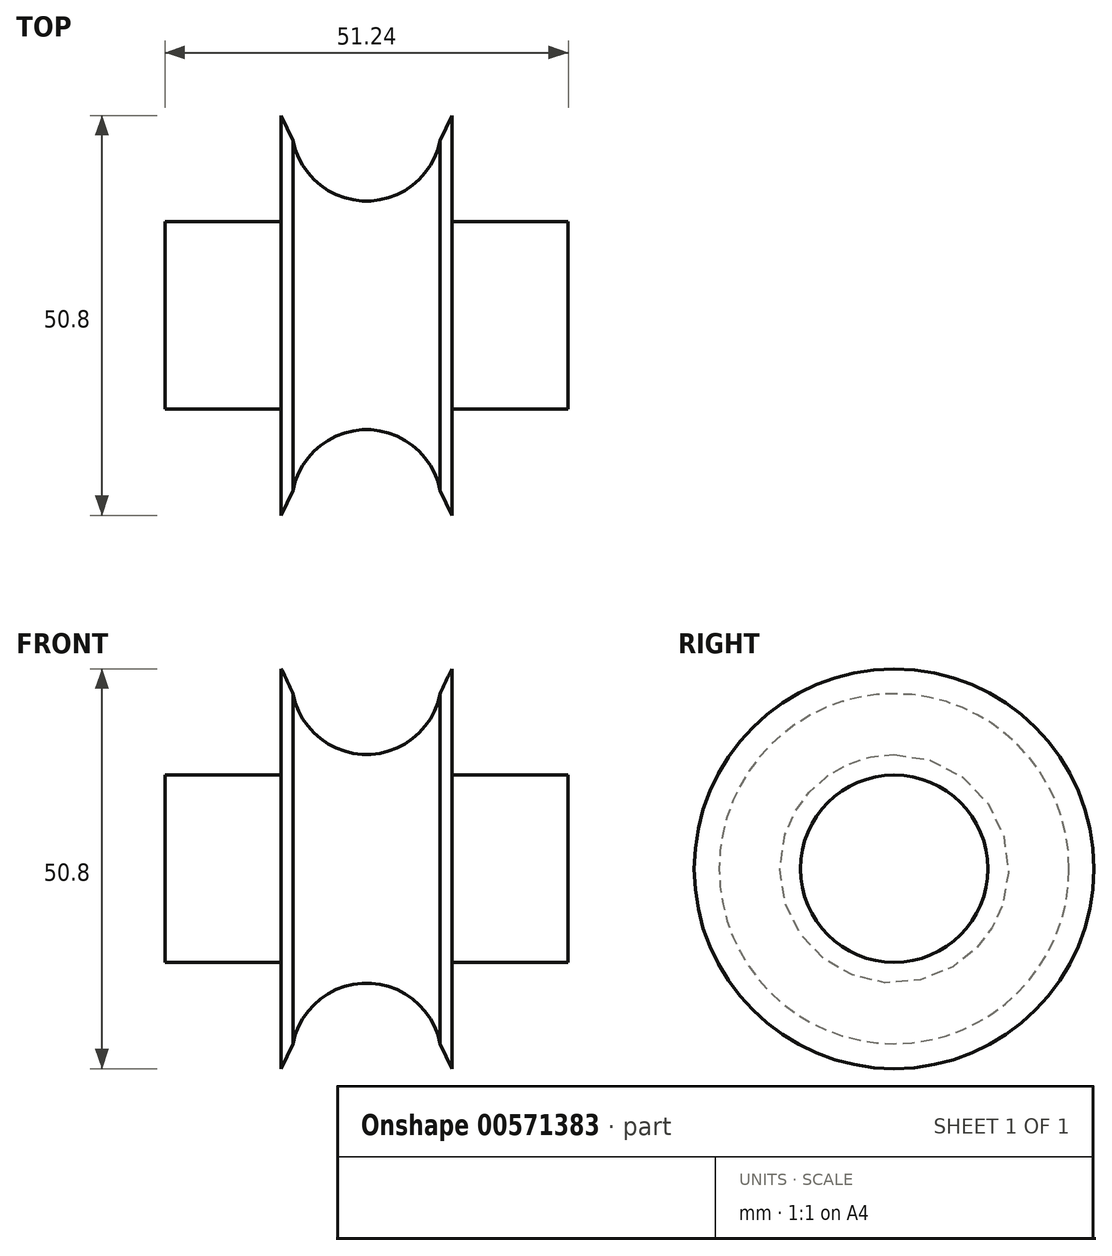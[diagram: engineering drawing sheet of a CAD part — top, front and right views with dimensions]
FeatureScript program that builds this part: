
annotation { "Feature Type Name" : "Feature", "Feature Type Description" : "" }
export const myFeature = defineFeature(function(context is Context, id is Id, definition is map)
    precondition{}
    {
        {
            var Q0;
            Q0=qCreatedBy(makeId("Front.planeOp"),FACE);
            var sketch = newSketch(context, id + "F0", { "sketchPlane" : qUnion([Q0])});
            skLineSegment(sketch, "E0", {"start": v(-10.83, 0) * mm, "end": v(0, 0) * mm});
            skLineSegment(sketch, "E1", {"start": v(-10.83, 25.4) * mm, "end": v(-10.83, 0) * mm});
            skLineSegment(sketch, "E2", {"start": v(-10.83, 11.9) * mm, "end": v(-25.62, 11.9) * mm});
            skLineSegment(sketch, "E3", {"start": v(-25.62, 11.9) * mm, "end": v(-25.62, 0) * mm});
            skLineSegment(sketch, "E4", {"start": v(-25.62, 0) * mm, "end": v(0, 0) * mm});
            skLineSegment(sketch, "E5", {"start": v(-10.83, 25.4) * mm, "end": v(-9.35, 22.23) * mm});
            skLineSegment(sketch, "E6.MirrorCS", {"start": v(25.62, 11.9) * mm, "end": v(25.62, 0) * mm});
            skLineSegment(sketch, "E7.MirrorCS", {"start": v(10.83, 11.9) * mm, "end": v(25.62, 11.9) * mm});
            skLineSegment(sketch, "E8.MirrorCS", {"start": v(10.83, 25.4) * mm, "end": v(10.83, 0) * mm});
            skLineSegment(sketch, "E9.MirrorCS", {"start": v(10.83, 25.4) * mm, "end": v(9.35, 22.23) * mm});
            skLineSegment(sketch, "E10.MirrorCS", {"start": v(25.62, 0) * mm, "end": v(0, 0) * mm});
            skArc(sketch, "E11", {"start": v(-9.35, 22.23) * mm, "mid": v(0, 14.52) * mm, "end": v(9.35, 22.23) * mm});
            skLineSegment(sketch, "E12", {"start": v(-37.22, 0) * mm, "end": v(46.88, 0) * mm, "construction": true});
            skSolve(sketch);
        }
        {
            var Q0;
            {var subQ0=sQuery(id+"F0.wireOp",EDGE,"E5");Q0=makeQuery(id+"F0.imprint","IMPRINT",FACE,{"disambiguationData":[TD([[makeQuery(id+"F0.imprint","IMPRINT",EDGE,{"derivedFrom":subQ0}),-1.0]])]});}
            var Q1;
            {var subQ0=sQuery(id+"F0.wireOp",EDGE,"E6.MirrorCS");Q1=makeQuery(id+"F0.imprint","IMPRINT",FACE,{"disambiguationData":[TD([[makeQuery(id+"F0.imprint","IMPRINT",EDGE,{"derivedFrom":subQ0}),-1.0]])]});}
            var Q2;
            {var subQ3=sQuery(id+"F0.wireOp",EDGE,"E2");Q2=makeQuery(id+"F0.imprint","IMPRINT",FACE,{"disambiguationData":[TD([[makeQuery(id+"F0.imprint","IMPRINT",EDGE,{"derivedFrom":subQ3}),1.0]])]});}
            var Q3;
            Q3=sQuery(id+"F0.wireOp",EDGE,"E12");
            revolve(context, id + "F1", {"entities" : qUnion([Q0, Q1, Q2]), "axis" : qUnion([Q3]), "revolveType" : RevolveType.FULL});
        }
    });
